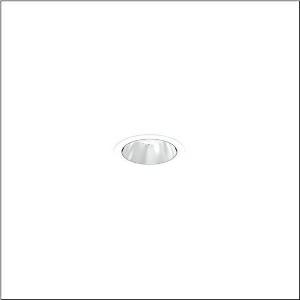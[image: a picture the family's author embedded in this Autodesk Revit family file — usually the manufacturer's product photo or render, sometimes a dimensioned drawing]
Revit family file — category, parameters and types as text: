
# Revit family: lunis_21_s_51db15ta91c
name_source: partatom
category: Lighting Fixtures
units: mm (PartAtom-declared; Revit-internal decimal feet)

## family parameters
Cut with Voids When Loaded = No
Host = Face
Light Source = No
Part Type = Normal
Room Calculation Point = No
Round Connector Dimension = Use Diameter
Shared = No

## types (1)
- --- (1 x LED 3000 K ... 6500 K, 1260 lm, 8 W, 4000K)
    Apparent Load = 8 VA
    CIE Flux Codes = 93 99 100 100 100
    Color Rendering = 80
    Color Temperature = 4000K
    Default Elevation = 1800 mm
    Description = Lunis 21,  S, downlight, light control with lens, of PMMA, anti glare with reflector, of PC, highly specular, light emission: direct distribution, LED rated luminous flux: 1.260lm, light colour: 8tw, with terminal, 5-pole, mains connection: 220..240V, AC, 50..60Hz, housing, round, of diecast aluminium, traffic white (RAL 9016), diameter: 84mm, clamping range: 1..40mm, protection rating (complete): IP20, protection rating (on room side): IP54, insulation class (complete): insulation class II (safety insulation), certification: CE, impact resistance: IK03, packaging unit: 1 piece
    Height = 0 mm  [stored 0 ft]
    Lamp = 1 x LED 3000 K ... 6500 K
    Lamp Light Flux = 1260 lm
    Lamp Power = 8 W
    Lamp count = 1
    Length = 84 mm
    Luminous efficacy = 158 lm/W
    Manufacturer = Siteco
    ModVariant = No
    Model = 51DB15TA91C
    Mounting Place = Ceiling
    Mounting Type = Recessed
    Number of Poles = 1
    OnlyDefault = Yes
    Power Factor = 1
    Product Name = Lunis 21 S
    Product group = downlight
    ProductGroupID = 400
    Protection Class = Protection class II
    Protection Degree = IP 20
    RLX_Detail_Level = 1
    RLX_Emergency_Light_Flux = 0 lm
    RLX_Emergency_Type = 0
    RLX_Emergency_Type_DB = No
    RlxData = <blob elided: 8517 chars, md5=196dad2a>
    Socket = socket
    Standby Power = 0 W
    System Light Flux = 1260 lm
    System Power = 8 W
    Type Comments = individual setting: CCT=4000K, colour temperature 4000K, luminous flux: 100 % | (OFF | OFF | ON | OFF) | 200 mA
    Type Image = l_1290840.jpg
    URL = http://relux.com
    VarID = @adj_020726
    Voltage = 0 V
    Weight = 0.00 kg
    Width = 0 mm  [stored 0 ft]

note: [stored X ft] marks values corroborated as IEEE doubles in the binary element streams (Revit-internal decimal feet)

## geometry (parser evidence)
native form markers: Sweep x8
no freeform markers — native parametric forms only
